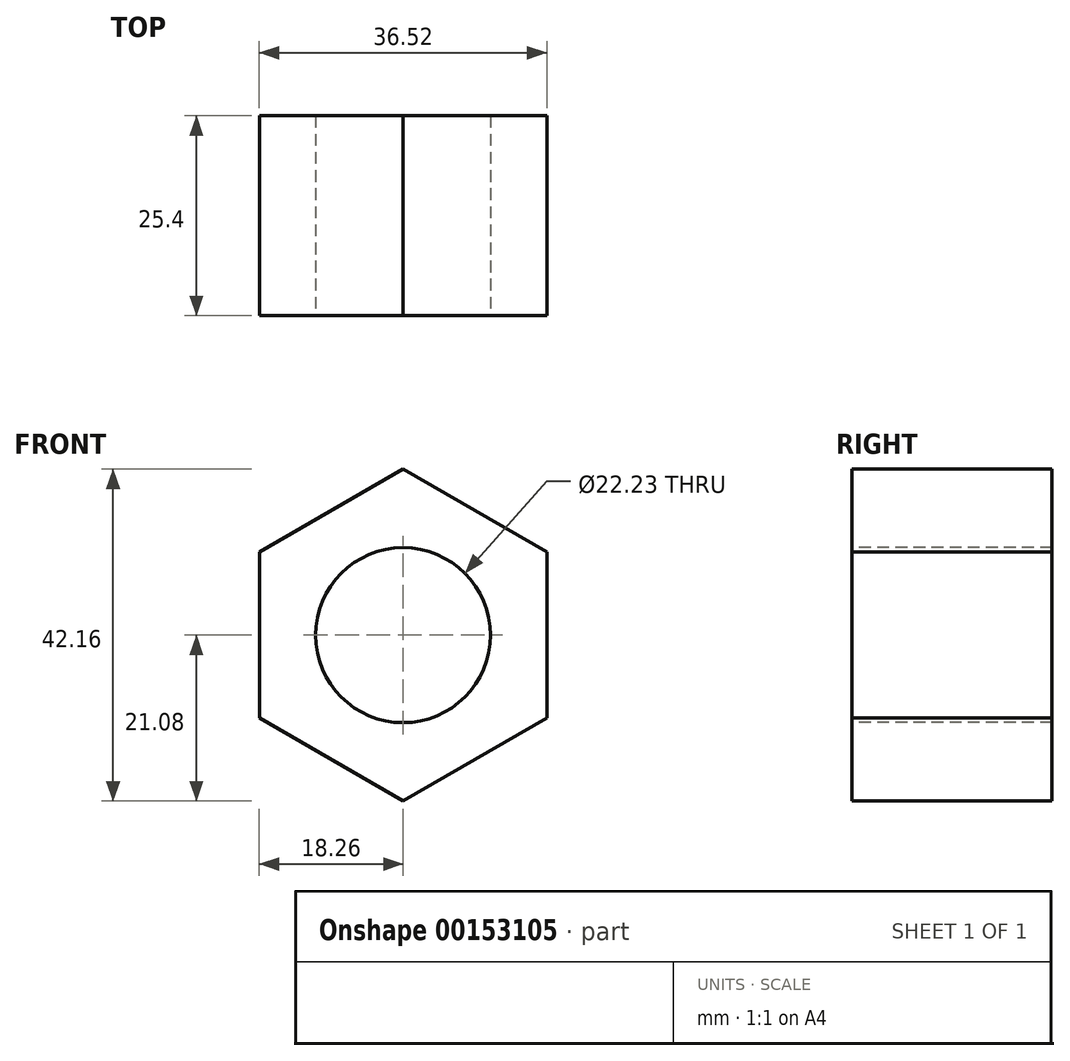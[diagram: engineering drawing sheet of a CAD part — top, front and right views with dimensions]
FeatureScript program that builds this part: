
annotation { "Feature Type Name" : "Feature", "Feature Type Description" : "" }
export const myFeature = defineFeature(function(context is Context, id is Id, definition is map)
    precondition{}
    {
        {
            var Q0;
            Q0=qCreatedBy(makeId("Front.planeOp"),FACE);
            var sketch = newSketch(context, id + "F0", { "sketchPlane" : qUnion([Q0])});
            skCircle(sketch, "E0.cCircle", {"center": v(0, 0) * mm, "radius": 18.26 * mm, "construction": true});
            skLineSegment(sketch, "E0.0", {"start": v(18.26, 10.54) * mm, "end": v(18.26, -10.54) * mm});
            skLineSegment(sketch, "E0.1", {"start": v(18.26, -10.54) * mm, "end": v(0, -21.08) * mm});
            skLineSegment(sketch, "E0.2", {"start": v(0, -21.08) * mm, "end": v(-18.26, -10.54) * mm});
            skLineSegment(sketch, "E0.3", {"start": v(-18.26, -10.54) * mm, "end": v(-18.26, 10.54) * mm});
            skLineSegment(sketch, "E0.4", {"start": v(-18.26, 10.54) * mm, "end": v(0, 21.08) * mm});
            skLineSegment(sketch, "E0.5", {"start": v(0, 21.08) * mm, "end": v(18.26, 10.54) * mm});
            skPoint(sketch, "E0.0.midPoint", {"position": v(18.26, 0) * mm});
            skSolve(sketch);
        }
        {
            var Q0;
            Q0=makeQuery(id+"F0.imprint","IMPRINT",FACE,{"disambiguationData":[TD([[makeQuery(id+"F0.imprint","IMPRINT",EDGE,{"derivedFrom":sQuery(id+"F0.wireOp",EDGE,"E0.0")}),-1.0]])]});
            extrude(context, id + "F1", {"entities" : qUnion([Q0]), "depth" : 25.4 * mm});
        }
        {
            var Q0;
            Q0=makeQuery(id+"F1.opExtrude","CAP_FACE",FACE,{"disambiguationData":[OSD([sQuery(id+"F0.wireOp",EDGE,"E0.0"),sQuery(id+"F0.wireOp",EDGE,"E0.1"),sQuery(id+"F0.wireOp",EDGE,"E0.2"),sQuery(id+"F0.wireOp",EDGE,"E0.3"),sQuery(id+"F0.wireOp",EDGE,"E0.4"),sQuery(id+"F0.wireOp",EDGE,"E0.5")])],"isStart":false});
            var sketch = newSketch(context, id + "F2", { "sketchPlane" : qUnion([Q0])});
            skPoint(sketch, "E1", {"position": v(0, 0) * mm});
            skSolve(sketch);
        }
        {
            var Q0;
            Q0=sQuery(id+"F2.wireOp",VERTEX,"E1");
            var Q1;
            Q1=makeQuery(id+"F1.opExtrude","SWEPT_BODY",BODY,{"disambiguationData":[OSD([sQuery(id+"F0.wireOp",EDGE,"E0.0"),sQuery(id+"F0.wireOp",EDGE,"E0.1"),sQuery(id+"F0.wireOp",EDGE,"E0.2"),sQuery(id+"F0.wireOp",EDGE,"E0.3"),sQuery(id+"F0.wireOp",EDGE,"E0.4"),sQuery(id+"F0.wireOp",EDGE,"E0.5")])]});
            hole(context, id + "F3", {"style" : HoleStyle.SIMPLE, "endStyle" : HoleEndStyle.THROUGH, "holeDiameter" : 22.22 * mm, "locations" : qUnion([Q0]), "scope" : qUnion([Q1]), "isTappedThrough" : true});
        }
    });
